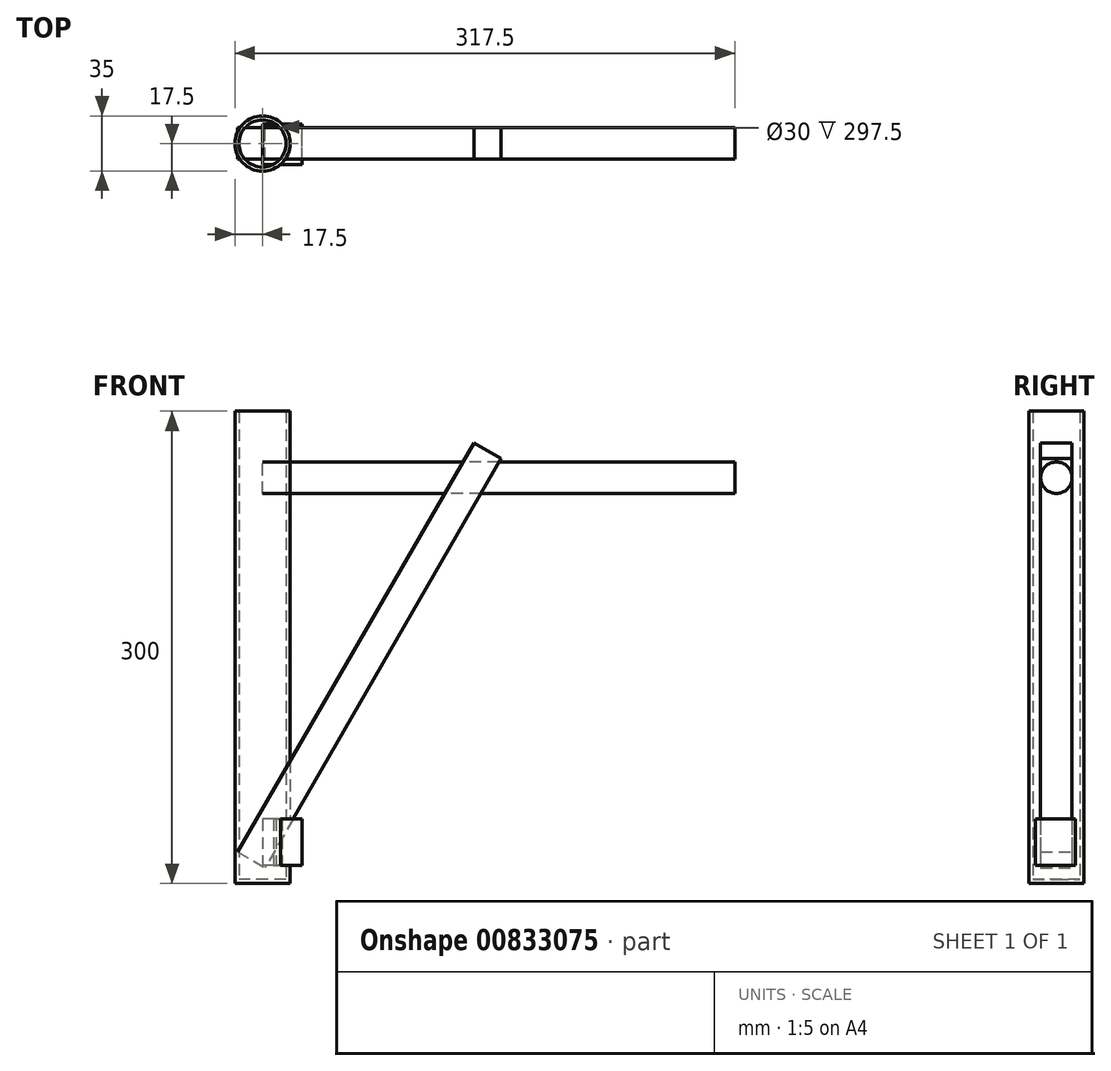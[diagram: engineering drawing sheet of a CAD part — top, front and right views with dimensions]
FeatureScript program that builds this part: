
annotation { "Feature Type Name" : "Feature", "Feature Type Description" : "" }
export const myFeature = defineFeature(function(context is Context, id is Id, definition is map)
    precondition{}
    {
        {
            var Q0;
            Q0=qCreatedBy(makeId("Top.planeOp"),FACE);
            var sketch = newSketch(context, id + "F0", { "sketchPlane" : qUnion([Q0])});
            skCircle(sketch, "E0", {"center": v(0, 0) * mm, "radius": 17.5 * mm});
            skSolve(sketch);
        }
        {
            var Q0;
            Q0=makeQuery(id+"F0.imprint","IMPRINT",FACE,{"disambiguationData":[TD([[makeQuery(id+"F0.imprint","IMPRINT",EDGE,{"derivedFrom":sQuery(id+"F0.wireOp",EDGE,"E0")}),1.0]])]});
            extrude(context, id + "F1", {"entities" : qUnion([Q0]), "depth" : 300 * mm, "offsetDistance" : 25 * mm});
        }
        {
            var Q0;
            Q0=makeQuery(id+"F1.opExtrude","CAP_FACE",FACE,{"disambiguationData":[OSD([sQuery(id+"F0.wireOp",EDGE,"E0")])],"isStart":false});
            shell(context, id + "F2", {"entities" : qUnion([Q0]), "thickness" : 2.5 * mm});
        }
        {
            var Q0;
            Q0=qCreatedBy(makeId("Right.planeOp"),FACE);
            var sketch = newSketch(context, id + "F3", { "sketchPlane" : qUnion([Q0])});
            skCircle(sketch, "E1", {"center": v(0, 257.75) * mm, "radius": 10 * mm});
            skSolve(sketch);
        }
        {
            var Q0;
            Q0 = qSketchRegion(id + "F3", true);
            extrude(context, id + "F4", {"entities" : qUnion([Q0]), "depth" : 300 * mm, "offsetDistance" : 25 * mm});
        }
        {
            var Q0;
            Q0=qCreatedBy(makeId("Right.planeOp"),FACE);
            var sketch = newSketch(context, id + "F5", { "sketchPlane" : qUnion([Q0])});
            skLineSegment(sketch, "E2.bottom", {"start": v(-13.3, 40.9) * mm, "end": v(12.23, 40.9) * mm});
            skLineSegment(sketch, "E2.top", {"start": v(-13.3, 11.6) * mm, "end": v(12.23, 11.6) * mm});
            skLineSegment(sketch, "E2.left", {"start": v(-13.3, 40.9) * mm, "end": v(-13.3, 11.6) * mm});
            skLineSegment(sketch, "E2.right", {"start": v(12.23, 40.9) * mm, "end": v(12.23, 11.6) * mm});
            skSolve(sketch);
        }
        {
            var Q0;
            Q0=qCreatedBy(makeId("Front.planeOp"),FACE);
            var sketch = newSketch(context, id + "F6", { "sketchPlane" : qUnion([Q0])});
            skLineSegment(sketch, "E3", {"start": v(0, 41.18) * mm, "end": v(11.61, 18.57) * mm});
            skSolve(sketch);
        }
        {
            var Q0;
            Q0 = qSketchRegion(id + "F5", true);
            extrude(context, id + "F7", {"entities" : qUnion([Q0]), "operationType" : NewBodyOperationType.ADD, "depth" : 25 * mm, "offsetDistance" : 25 * mm});
        }
        {
            var Q0;
            Q0=qCreatedBy(makeId("Right.planeOp"),FACE);
            var sketch = newSketch(context, id + "F8", { "sketchPlane" : qUnion([Q0])});
            skLineSegment(sketch, "E4", {"start": v(-109.11, 10.93) * mm, "end": v(110.3, 10.93) * mm});
            skSolve(sketch);
        }
        {
            var Q0;
            Q0=qCreatedBy(makeId("Top.planeOp"),FACE);
            var Q1;
            Q1=sQuery(id+"F8.wireOp",EDGE,"E4");
            cPlane(context, id + "F9", {"entities" : qUnion([Q0, Q1]), "cplaneType" : CPlaneType.LINE_ANGLE, "offset" : 25 * mm, "angle" : 30 * degree, "width" : 150 * mm, "height" : 150 * mm});
        }
        {
            var Q0;
            Q0=qCreatedBy(id+"F9.planeOp",FACE);
            var sketch = newSketch(context, id + "F10", { "sketchPlane" : qUnion([Q0])});
            skLineSegment(sketch, "E5.bottom", {"start": v(-23.65, 10) * mm, "end": v(-3.65, 10) * mm});
            skLineSegment(sketch, "E5.top", {"start": v(-23.65, -10) * mm, "end": v(-3.65, -10) * mm});
            skLineSegment(sketch, "E5.left", {"start": v(-23.65, 10) * mm, "end": v(-23.65, -10) * mm});
            skLineSegment(sketch, "E5.right", {"start": v(-3.65, 10) * mm, "end": v(-3.65, -10) * mm});
            skSolve(sketch);
        }
        {
            var Q0;
            Q0=makeQuery(id+"F10.imprint","IMPRINT",FACE,{"disambiguationData":[TD([[makeQuery(id+"F10.imprint","IMPRINT",EDGE,{"derivedFrom":sQuery(id+"F10.wireOp",EDGE,"E5.bottom")}),-1.0]])]});
            extrude(context, id + "F11", {"entities" : qUnion([Q0]), "oppositeDirection" : true, "depth" : 300 * mm, "offsetDistance" : 25 * mm});
        }
    });
